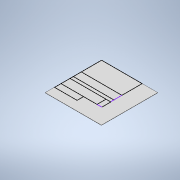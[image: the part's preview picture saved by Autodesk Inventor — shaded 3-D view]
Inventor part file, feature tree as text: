
AUTODESK INVENTOR PART (.ipt)
format: ipt  version: 2022 (Build 260153000, 153)  size: 112,128 bytes
history: native  units: mm
features: sketch x2, other x1, extrude x1
ambient origin geometry x8: Origin, YZ Plane, XZ Plane, XY Plane, X Axis, Y Axis, Z Axis, Center Point
bodies: Body1 (feature_tree)
feature tree (4):
  other  "ソリッド1"
  extrude  "押し出し1"  Depth=500.0mm
  sketch  "スケッチ2"
  sketch  "スケッチ1"
